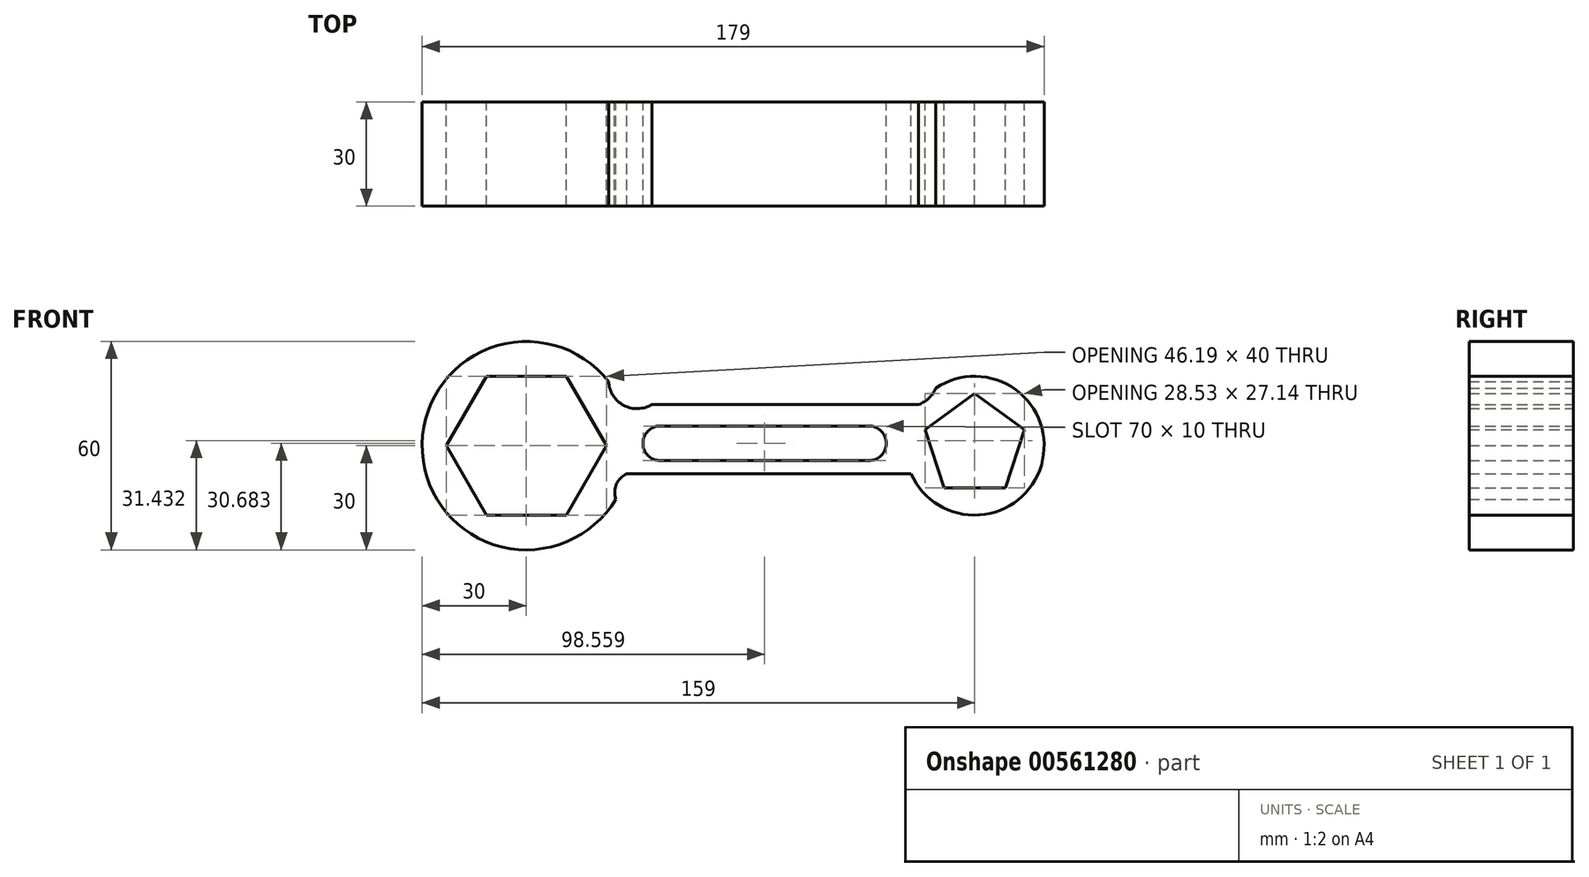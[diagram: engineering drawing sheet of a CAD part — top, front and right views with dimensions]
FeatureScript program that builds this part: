
annotation { "Feature Type Name" : "Feature", "Feature Type Description" : "" }
export const myFeature = defineFeature(function(context is Context, id is Id, definition is map)
    precondition{}
    {
        {
            var Q0;
            Q0=qCreatedBy(makeId("Front.planeOp"),FACE);
            var sketch = newSketch(context, id + "F0", { "sketchPlane" : qUnion([Q0])});
            skArc(sketch, "E0", {"start": v(-79.28, 18.47) * mm, "mid": v(-132.86, -1.87) * mm, "end": v(-77.17, -15.4) * mm});
            skArc(sketch, "E1", {"start": v(10, 11.88) * mm, "mid": v(39.91, -14.45) * mm, "end": v(14.9, 16.59) * mm});
            skLineSegment(sketch, "E2", {"start": v(6.08, 0) * mm, "end": v(46.08, 0) * mm});
            skLineSegment(sketch, "E3", {"start": v(-66.77, 11.88) * mm, "end": v(10, 11.88) * mm});
            skLineSegment(sketch, "E4", {"start": v(-74.04, -8.12) * mm, "end": v(7.8, -8.12) * mm});
            skCircle(sketch, "E5.cCircle", {"center": v(-102.92, 0) * mm, "radius": 20 * mm, "construction": true});
            skLineSegment(sketch, "E5.0", {"start": v(-114.47, 20) * mm, "end": v(-91.37, 20) * mm});
            skLineSegment(sketch, "E5.1", {"start": v(-91.37, 20) * mm, "end": v(-79.83, 0) * mm});
            skLineSegment(sketch, "E5.2", {"start": v(-79.83, 0) * mm, "end": v(-91.37, -20) * mm});
            skLineSegment(sketch, "E5.3", {"start": v(-91.37, -20) * mm, "end": v(-114.47, -20) * mm});
            skLineSegment(sketch, "E5.4", {"start": v(-114.47, -20) * mm, "end": v(-126.01, 0) * mm});
            skLineSegment(sketch, "E5.5", {"start": v(-126.01, 0) * mm, "end": v(-114.47, 20) * mm});
            skPoint(sketch, "E5.0.midPoint", {"position": v(-102.92, 20) * mm});
            skCircle(sketch, "E6.cCircle", {"center": v(26.08, 0) * mm, "radius": 12.14 * mm, "construction": true});
            skLineSegment(sketch, "E6.0", {"start": v(34.9, -12.14) * mm, "end": v(17.26, -12.14) * mm});
            skLineSegment(sketch, "E6.1", {"start": v(17.26, -12.14) * mm, "end": v(11.81, 4.64) * mm});
            skLineSegment(sketch, "E6.2", {"start": v(11.81, 4.64) * mm, "end": v(26.08, 15) * mm});
            skLineSegment(sketch, "E6.3", {"start": v(26.08, 15) * mm, "end": v(40.35, 4.64) * mm});
            skLineSegment(sketch, "E6.4", {"start": v(40.35, 4.64) * mm, "end": v(34.9, -12.14) * mm});
            skPoint(sketch, "E6.0.midPoint", {"position": v(26.08, -12.14) * mm});
            skLineSegment(sketch, "E7.bottom", {"start": v(-64.36, 5.68) * mm, "end": v(-4.36, 5.68) * mm});
            skLineSegment(sketch, "E7.top", {"start": v(-64.36, -4.32) * mm, "end": v(-4.36, -4.32) * mm});
            skLineSegment(sketch, "E7.left", {"start": v(-69.36, 0.68) * mm, "end": v(-69.36, 0.68) * mm});
            skLineSegment(sketch, "E7.right", {"start": v(0.64, 0.68) * mm, "end": v(0.64, 0.68) * mm});
            skPoint(sketch, "E8.visualSharp", {"position": v(-69.36, 5.68) * mm});
            skArc(sketch, "E8.filletArc", {"start": v(-64.36, 5.68) * mm, "mid": v(-67.9, 4.22) * mm, "end": v(-69.36, 0.68) * mm});
            skPoint(sketch, "E9.visualSharp", {"position": v(-69.36, -4.32) * mm});
            skArc(sketch, "E9.filletArc", {"start": v(-69.36, 0.68) * mm, "mid": v(-67.9, -2.85) * mm, "end": v(-64.36, -4.32) * mm});
            skPoint(sketch, "E10.visualSharp", {"position": v(0.64, -4.32) * mm});
            skArc(sketch, "E10.filletArc", {"start": v(-4.36, -4.32) * mm, "mid": v(-0.83, -2.85) * mm, "end": v(0.64, 0.68) * mm});
            skPoint(sketch, "E11.visualSharp", {"position": v(0.64, 5.68) * mm});
            skArc(sketch, "E11.filletArc", {"start": v(0.64, 0.68) * mm, "mid": v(-0.83, 4.22) * mm, "end": v(-4.36, 5.68) * mm});
            skArc(sketch, "E12", {"start": v(-79.28, 18.47) * mm, "mid": v(-74.9, 11.61) * mm, "end": v(-66.77, 11.88) * mm});
            skArc(sketch, "E13", {"start": v(-69.36, -8.12) * mm, "mid": v(-75.66, -9.19) * mm, "end": v(-77.17, -15.4) * mm});
            skArc(sketch, "E14.trimOffspring", {"start": v(-74.04, -8.12) * mm, "mid": v(-72.99, 2) * mm, "end": v(-75.37, 11.88) * mm});
            skArc(sketch, "E15", {"start": v(4.32, 11.88) * mm, "mid": v(10.56, 12.1) * mm, "end": v(14.9, 16.59) * mm});
            skArc(sketch, "E16", {"start": v(10, -11.88) * mm, "mid": v(7.37, -7.87) * mm, "end": v(2.6, -8.12) * mm});
            skSolve(sketch);
        }
        {
            var Q0;
            Q0 = qSketchRegion(id + "F0", true);
            extrude(context, id + "F1", {"entities" : qUnion([Q0]), "depth" : 30 * mm, "offsetDistance" : 25 * mm});
        }
    });
